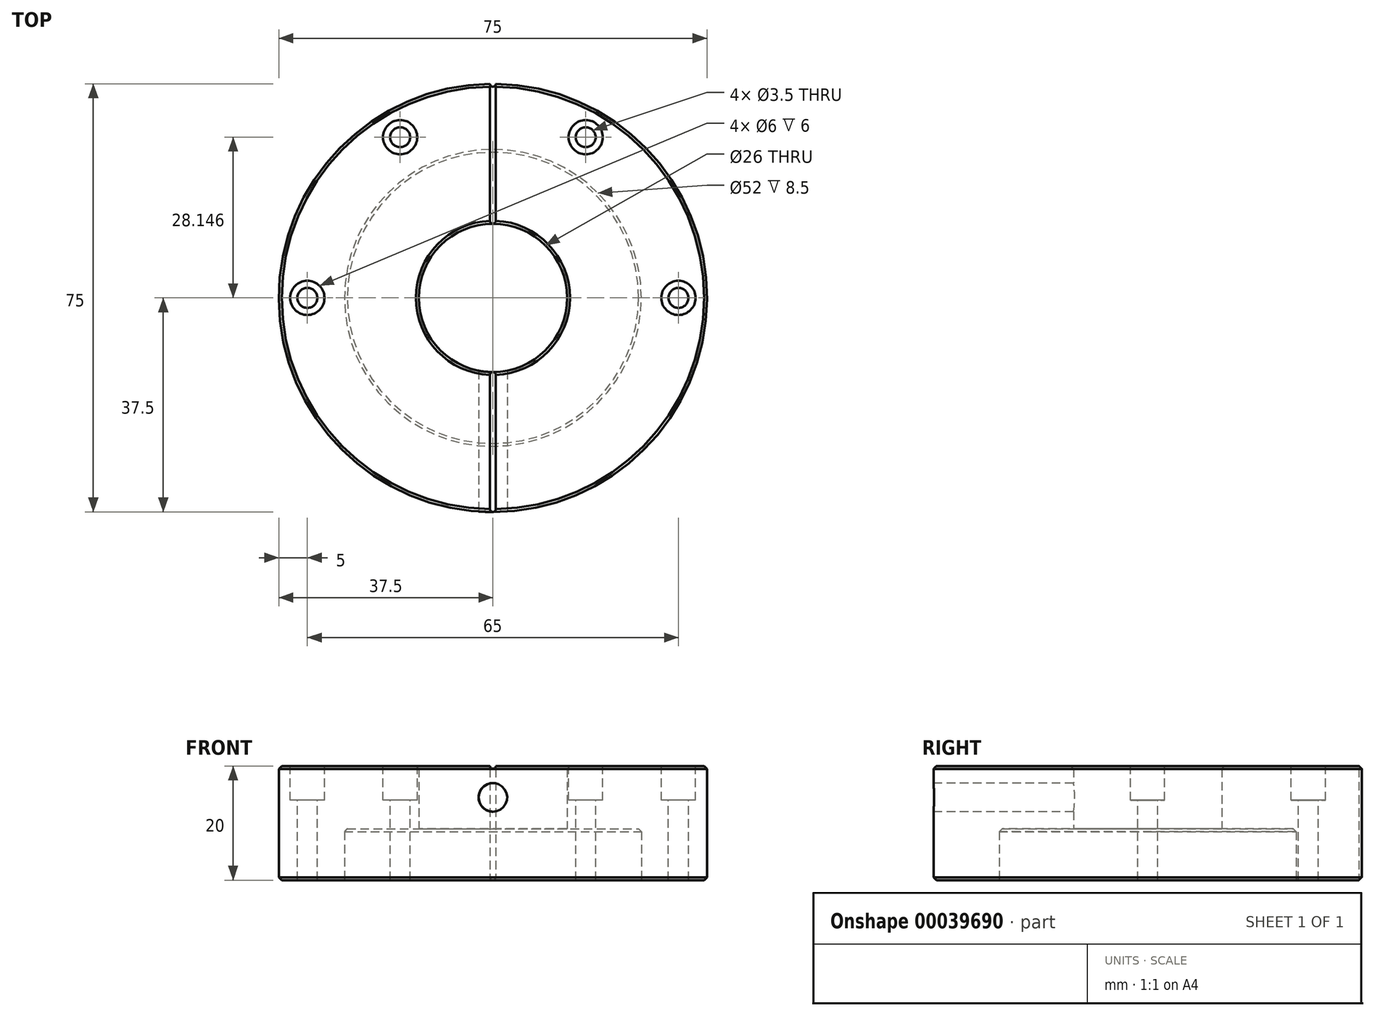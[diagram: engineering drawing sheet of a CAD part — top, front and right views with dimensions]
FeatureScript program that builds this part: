
annotation { "Feature Type Name" : "Feature", "Feature Type Description" : "" }
export const myFeature = defineFeature(function(context is Context, id is Id, definition is map)
    precondition{}
    {
        {
            var Q0;
            Q0=qCreatedBy(makeId("Top.planeOp"),FACE);
            var sketch = newSketch(context, id + "F0", { "sketchPlane" : qUnion([Q0])});
            skCircle(sketch, "E0", {"center": v(0, 0) * mm, "radius": 13 * mm});
            skCircle(sketch, "E1", {"center": v(0, 0) * mm, "radius": 37.5 * mm});
            skSolve(sketch);
        }
        {
            var Q0;
            Q0=makeQuery(id+"F0.imprint","IMPRINT",FACE,{"disambiguationData":[TD([[makeQuery(id+"F0.imprint","IMPRINT",EDGE,{"derivedFrom":sQuery(id+"F0.wireOp",EDGE,"E0")}),-1.0]])]});
            extrude(context, id + "F1", {"entities" : qUnion([Q0]), "depth" : 20 * mm});
        }
        {
            var Q0;
            Q0=makeQuery(id+"F1.opExtrude","CAP_FACE",FACE,{"disambiguationData":[OSD([sQuery(id+"F0.wireOp",EDGE,"E0"),sQuery(id+"F0.wireOp",EDGE,"E1")])],"isStart":true});
            var sketch = newSketch(context, id + "F2", { "sketchPlane" : qUnion([Q0])});
            skCircle(sketch, "E2", {"center": v(0, 0) * mm, "radius": 26 * mm});
            skSolve(sketch);
        }
        {
            var Q0;
            Q0=makeQuery(id+"F2.imprint","IMPRINT",FACE,{"disambiguationData":[TD([[makeQuery(id+"F2.imprint","IMPRINT",EDGE,{"derivedFrom":sQuery(id+"F2.wireOp",EDGE,"E2")}),1.0]])]});
            extrude(context, id + "F3", {"entities" : qUnion([Q0]), "operationType" : NewBodyOperationType.REMOVE, "oppositeDirection" : true, "depth" : 9 * mm});
        }
        {
            var Q0;
            Q0=makeQuery(id+"F1.opExtrude","CAP_FACE",FACE,{"disambiguationData":[OSD([sQuery(id+"F0.wireOp",EDGE,"E0"),sQuery(id+"F0.wireOp",EDGE,"E1")])],"isStart":false});
            var sketch = newSketch(context, id + "F4", { "sketchPlane" : qUnion([Q0])});
            skPoint(sketch, "E3", {"position": v(32.5, 0) * mm});
            skPoint(sketch, "E4.1.0", {"position": v(16.25, 28.15) * mm});
            skPoint(sketch, "E4.2.0", {"position": v(-16.25, 28.15) * mm});
            skPoint(sketch, "E4.3.0", {"position": v(-32.5, 0) * mm});
            skPoint(sketch, "E4.center", {"position": v(0, 0) * mm});
            skLineSegment(sketch, "E4.anchor1", {"start": v(0, 0) * mm, "end": v(32.5, 0) * mm, "construction": true});
            skLineSegment(sketch, "E4.anchor2", {"start": v(0, 0) * mm, "end": v(-32.5, 0) * mm, "construction": true});
            skSolve(sketch);
        }
        {
            var Q0;
            Q0=sQuery(id+"F4.wireOp",VERTEX,"E3");
            var Q1;
            Q1=sQuery(id+"F4.wireOp",VERTEX,"E4.1.0");
            var Q2;
            Q2=sQuery(id+"F4.wireOp",VERTEX,"E4.2.0");
            var Q3;
            Q3=sQuery(id+"F4.wireOp",VERTEX,"E4.3.0");
            var Q4;
            Q4=makeQuery(id+"F1.opExtrude","SWEPT_BODY",BODY,{"disambiguationData":[OSD([sQuery(id+"F0.wireOp",EDGE,"E0"),sQuery(id+"F0.wireOp",EDGE,"E1")])]});
            hole(context, id + "F5", {"style" : HoleStyle.C_BORE, "holeDiameter" : 3.5 * mm, "cBoreDiameter" : 6 * mm, "cBoreDepth" : 6 * mm, "endStyle" : HoleEndStyle.THROUGH, "locations" : qUnion([Q0, Q1, Q2, Q3]), "scope" : qUnion([Q4])});
        }
        {
            var Q0;
            Q0=qCreatedBy(makeId("Front.planeOp"),FACE);
            cPlane(context, id + "F6", {"entities" : qUnion([Q0]), "cplaneType" : CPlaneType.OFFSET, "offset" : 37.5 * mm, "width" : 150 * mm, "height" : 150 * mm});
        }
        {
            var Q0;
            Q0=qCreatedBy(id+"F6.planeOp",FACE);
            var sketch = newSketch(context, id + "F7", { "sketchPlane" : qUnion([Q0])});
            skPoint(sketch, "E5", {"position": v(0, 14.5) * mm});
            skSolve(sketch);
        }
        {
            var Q0;
            Q0=sQuery(id+"F7.wireOp",VERTEX,"E5");
            var Q1;
            Q1=makeQuery(id+"F1.opExtrude","SWEPT_BODY",BODY,{"disambiguationData":[OSD([sQuery(id+"F0.wireOp",EDGE,"E0"),sQuery(id+"F0.wireOp",EDGE,"E1")])]});
            hole(context, id + "F8", {"style" : HoleStyle.SIMPLE, "holeDiameter" : 5 * mm, "endStyle" : HoleEndStyle.BLIND, "holeDepth" : 35 * mm, "locations" : qUnion([Q0]), "scope" : qUnion([Q1])});
        }
        {
            var Q0;
            Q0=qCreatedBy(makeId("Front.planeOp"),FACE);
            var sketch = newSketch(context, id + "F9", { "sketchPlane" : qUnion([Q0])});
            skCircle(sketch, "E6", {"center": v(0, 20) * mm, "radius": 0.5 * mm});
            skSolve(sketch);
        }
        {
            var Q0;
            Q0=makeQuery(id+"F9.imprint","IMPRINT",FACE,{"disambiguationData":[TD([[makeQuery(id+"F9.imprint","IMPRINT",EDGE,{"derivedFrom":sQuery(id+"F9.wireOp",EDGE,"E6")}),1.0]])]});
            extrude(context, id + "F10", {"entities" : qUnion([Q0]), "operationType" : NewBodyOperationType.REMOVE, "endBound" : BoundingType.THROUGH_ALL, "oppositeDirection" : true, "depth" : 25 * mm, "hasSecondDirection" : true, "secondDirectionBound" : SecondDirectionBoundingType.THROUGH_ALL, "secondDirectionOppositeDirection" : false, "secondDirectionDepth" : 25 * mm});
        }
        {
            var Q0;
            Q0=qCreatedBy(makeId("Top.planeOp"),FACE);
            var sketch = newSketch(context, id + "F11", { "sketchPlane" : qUnion([Q0])});
            skCircle(sketch, "E7", {"center": v(0, 37.5) * mm, "radius": 0.5 * mm});
            skSolve(sketch);
        }
        {
            var Q0;
            Q0=makeQuery(id+"F11.imprint","IMPRINT",FACE,{"disambiguationData":[TD([[makeQuery(id+"F11.imprint","IMPRINT",EDGE,{"derivedFrom":sQuery(id+"F11.wireOp",EDGE,"E7")}),1.0]])]});
            extrude(context, id + "F12", {"entities" : qUnion([Q0]), "operationType" : NewBodyOperationType.REMOVE, "depth" : 25 * mm});
        }
        {
            var Q0;
            Q0=makeQuery(id+"F10.boolean.opBoolean","SPLIT",EDGE,{"disambiguationData":[OD(1.0)],"derivedFrom":makeQuery(id+"F1.opExtrude","CAP_EDGE",EDGE,{"disambiguationData":[OSD([sQuery(id+"F0.wireOp",EDGE,"E0")])],"isStart":false})});
            var Q1;
            Q1=makeQuery(id+"F10.boolean.opBoolean","SPLIT",EDGE,{"disambiguationData":[OD(0.0)],"derivedFrom":makeQuery(id+"F1.opExtrude","CAP_EDGE",EDGE,{"disambiguationData":[OSD([sQuery(id+"F0.wireOp",EDGE,"E0")])],"isStart":false})});
            var Q2;
            Q2=makeQuery(id+"F10.boolean.opBoolean","SPLIT",EDGE,{"disambiguationData":[OD(0.0)],"derivedFrom":makeQuery(id+"F1.opExtrude","CAP_EDGE",EDGE,{"disambiguationData":[OSD([sQuery(id+"F0.wireOp",EDGE,"E1")])],"isStart":false})});
            var Q3;
            Q3=makeQuery(id+"F10.boolean.opBoolean","SPLIT",EDGE,{"disambiguationData":[OD(1.0)],"derivedFrom":makeQuery(id+"F1.opExtrude","CAP_EDGE",EDGE,{"disambiguationData":[OSD([sQuery(id+"F0.wireOp",EDGE,"E1")])],"isStart":false})});
            var Q4;
            Q4=makeQuery(id+"F1.opExtrude","CAP_EDGE",EDGE,{"disambiguationData":[OSD([sQuery(id+"F0.wireOp",EDGE,"E1")])],"isStart":true});
            var Q5;
            Q5=makeQuery(id+"F3.boolean.opBoolean","COPY",EDGE,{"derivedFrom":makeQuery(id+"F3.opExtrude","CAP_EDGE",EDGE,{"disambiguationData":[OSD([sQuery(id+"F2.wireOp",EDGE,"E2")])],"isStart":true})});
            var Q6;
            Q6=makeQuery(id+"F3.boolean.opBoolean","COPY",EDGE,{"derivedFrom":makeQuery(id+"F3.opExtrude","CAP_EDGE",EDGE,{"disambiguationData":[OSD([sQuery(id+"F2.wireOp",EDGE,"E2")])],"isStart":false})});
            var Q7;
            Q7=makeQuery(id+"F3.boolean.opBoolean","COPY",EDGE,{"derivedFrom":makeQuery(id+"F3.opExtrude","CAP_EDGE",EDGE,{"disambiguationData":[OSD([sQuery(id+"F0.wireOp",EDGE,"E0")])],"isStart":false})});
            chamfer(context, id + "F13", {"entities" : qUnion([Q0, Q1, Q2, Q3, Q4, Q5, Q6, Q7]), "width" : 0.5 * mm, "tangentPropagation" : true});
        }
    });
